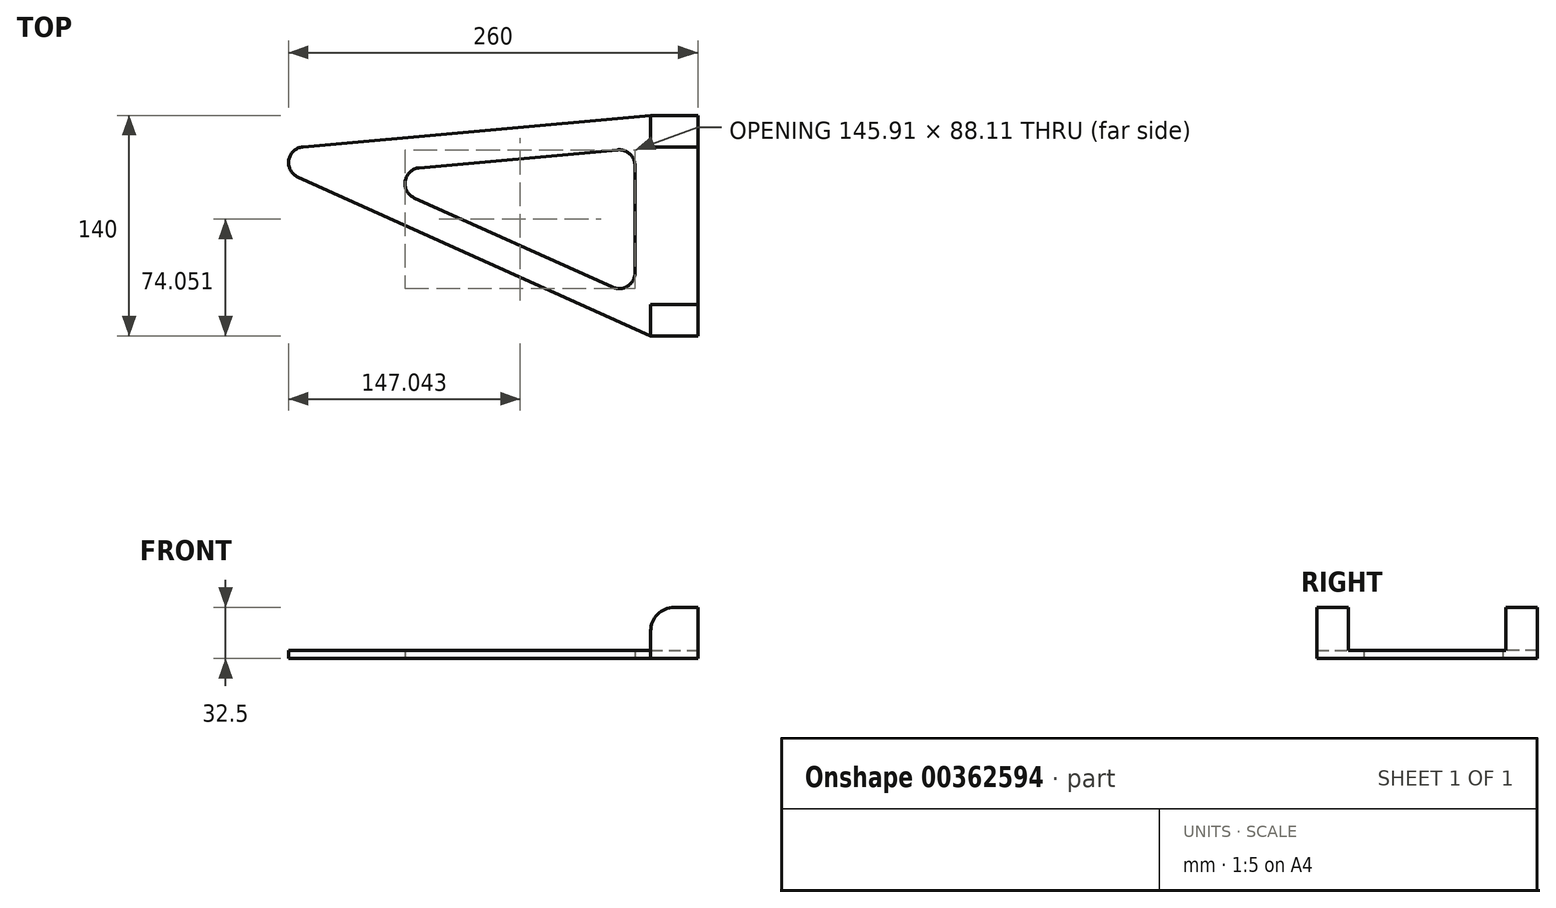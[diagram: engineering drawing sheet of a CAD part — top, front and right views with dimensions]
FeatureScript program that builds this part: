
annotation { "Feature Type Name" : "Feature", "Feature Type Description" : "" }
export const myFeature = defineFeature(function(context is Context, id is Id, definition is map)
    precondition{}
    {
        {
            var Q0;
            Q0=qCreatedBy(makeId("Top.planeOp"),FACE);
            var sketch = newSketch(context, id + "F0", { "sketchPlane" : qUnion([Q0])});
            skLineSegment(sketch, "E0", {"start": v(0, 32.72) * mm, "end": v(-250.9, 9.96) * mm});
            skLineSegment(sketch, "E1", {"start": v(-254.1, -9.12) * mm, "end": v(0, -123.5) * mm});
            skLineSegment(sketch, "E2", {"start": v(0, -123.5) * mm, "end": v(0, 32.72) * mm});
            skLineSegment(sketch, "E3.bottom", {"start": v(0, 10) * mm, "end": v(-30, 10) * mm});
            skLineSegment(sketch, "E3.top", {"start": v(0, 30) * mm, "end": v(-30, 30) * mm});
            skLineSegment(sketch, "E3.left", {"start": v(0, 10) * mm, "end": v(0, 30) * mm});
            skLineSegment(sketch, "E3.right", {"start": v(-30, 10) * mm, "end": v(-30, 30) * mm});
            skLineSegment(sketch, "E4.bottom", {"start": v(0, -90) * mm, "end": v(-30, -90) * mm});
            skLineSegment(sketch, "E4.top", {"start": v(0, -110) * mm, "end": v(-30, -110) * mm});
            skLineSegment(sketch, "E4.left", {"start": v(0, -90) * mm, "end": v(0, -110) * mm});
            skLineSegment(sketch, "E4.right", {"start": v(-30, -90) * mm, "end": v(-30, -110) * mm});
            skCircle(sketch, "E5", {"center": v(-250, 0) * mm, "radius": 10 * mm});
            skLineSegment(sketch, "E6", {"start": v(-30, 10) * mm, "end": v(-214.89, -6.77) * mm, "construction": true});
            skLineSegment(sketch, "E7", {"start": v(-214.89, -6.77) * mm, "end": v(-30, -90) * mm, "construction": true});
            skPoint(sketch, "E8.visualSharp", {"position": v(-214.89, -6.77) * mm});
            skLineSegment(sketch, "E9", {"start": v(-30, 10) * mm, "end": v(-30, -90) * mm});
            skLineSegment(sketch, "E10", {"start": v(-40, -1.86) * mm, "end": v(-40, -70.03) * mm});
            skLineSegment(sketch, "E11", {"start": v(-176.95, -3.33) * mm, "end": v(-50.9, 8.1) * mm});
            skLineSegment(sketch, "E12", {"start": v(-180.15, -22.4) * mm, "end": v(-54.1, -79.15) * mm});
            skPoint(sketch, "E13.visualSharp", {"position": v(-40, 9.1) * mm});
            skArc(sketch, "E13.filletArc", {"start": v(-40, -1.86) * mm, "mid": v(-43.26, 5.53) * mm, "end": v(-50.9, 8.1) * mm});
            skPoint(sketch, "E14.visualSharp", {"position": v(-40, -85.5) * mm});
            skArc(sketch, "E15.filletArc", {"start": v(-176.95, -3.33) * mm, "mid": v(-185.9, -11.64) * mm, "end": v(-180.15, -22.4) * mm});
            skArc(sketch, "E16.filletArc", {"start": v(-54.1, -79.15) * mm, "mid": v(-44.57, -78.43) * mm, "end": v(-40, -70.03) * mm});
            skSolve(sketch);
        }
        {
            var Q0;
            {var subQ5=sQuery(id+"F0.wireOp",EDGE,"E3.right");Q0=makeQuery(id+"F0.imprint","IMPRINT",FACE,{"disambiguationData":[TD([[makeQuery(id+"F0.imprint","IMPRINT",EDGE,{"derivedFrom":subQ5}),1.0]])]});}
            var Q1;
            {var subQ0=sQuery(id+"F0.wireOp",EDGE,"E5");var subQ1=makeQuery(id+"F0.imprint","INTERSECT",VERTEX,{"derivedFrom":[sQuery(id+"F0.wireOp",EDGE,"E0"),subQ0]});Q1=makeQuery(id+"F0.imprint","IMPRINT",FACE,{"disambiguationData":[TD([[makeQuery(id+"F0.imprint","IMPRINT",EDGE,{"disambiguationData":[TD([[subQ1,-1.0]])],"derivedFrom":subQ0}),1.0]])]});}
            var Q2;
            Q2=makeQuery(id+"F0.imprint","IMPRINT",FACE,{"disambiguationData":[TD([[makeQuery(id+"F0.imprint","IMPRINT",EDGE,{"derivedFrom":sQuery(id+"F0.wireOp",EDGE,"E3.bottom")}),-1.0]])]});
            var Q3;
            {var subQ0=sQuery(id+"F0.wireOp",EDGE,"E3.bottom");Q3=makeQuery(id+"F0.imprint","IMPRINT",FACE,{"disambiguationData":[TD([[makeQuery(id+"F0.imprint","IMPRINT",EDGE,{"derivedFrom":subQ0}),1.0]])]});}
            var Q4;
            Q4=makeQuery(id+"F0.imprint","IMPRINT",FACE,{"disambiguationData":[TD([[makeQuery(id+"F0.imprint","IMPRINT",EDGE,{"derivedFrom":sQuery(id+"F0.wireOp",EDGE,"E4.bottom")}),1.0]])]});
            extrude(context, id + "F1", {"entities" : qUnion([Q0, Q1, Q2, Q3, Q4]), "endBound" : BoundingType.SYMMETRIC, "depth" : 5 * mm});
        }
        {
            var Q0;
            Q0=makeQuery(id+"F0.imprint","IMPRINT",FACE,{"disambiguationData":[TD([[makeQuery(id+"F0.imprint","IMPRINT",EDGE,{"derivedFrom":sQuery(id+"F0.wireOp",EDGE,"E3.bottom")}),-1.0]])]});
            var Q1;
            Q1=makeQuery(id+"F0.imprint","IMPRINT",FACE,{"disambiguationData":[TD([[makeQuery(id+"F0.imprint","IMPRINT",EDGE,{"derivedFrom":sQuery(id+"F0.wireOp",EDGE,"E4.bottom")}),1.0]])]});
            extrude(context, id + "F2", {"entities" : qUnion([Q0, Q1]), "operationType" : NewBodyOperationType.ADD, "depth" : 30 * mm});
        }
        {
            var Q0;
            Q0=makeQuery(id+"F2.opExtrude","CAP_EDGE",EDGE,{"disambiguationData":[OSD([sQuery(id+"F0.wireOp",EDGE,"E3.left")])],"isStart":false});
            var Q1;
            Q1=makeQuery(id+"F2.opExtrude","CAP_EDGE",EDGE,{"disambiguationData":[OSD([sQuery(id+"F0.wireOp",EDGE,"E3.right")])],"isStart":false});
            var Q2;
            Q2=makeQuery(id+"F2.opExtrude","CAP_EDGE",EDGE,{"disambiguationData":[OSD([sQuery(id+"F0.wireOp",EDGE,"E4.left")])],"isStart":false});
            var Q3;
            Q3=makeQuery(id+"F2.opExtrude","CAP_EDGE",EDGE,{"disambiguationData":[OSD([sQuery(id+"F0.wireOp",EDGE,"E4.right")])],"isStart":false});
            fillet(context, id + "F3", {"entities" : qUnion([Q0, Q1, Q2, Q3]), "radius" : 15 * mm, "tangentPropagation" : true, "allowEdgeOverflow" : false});
        }
    });
